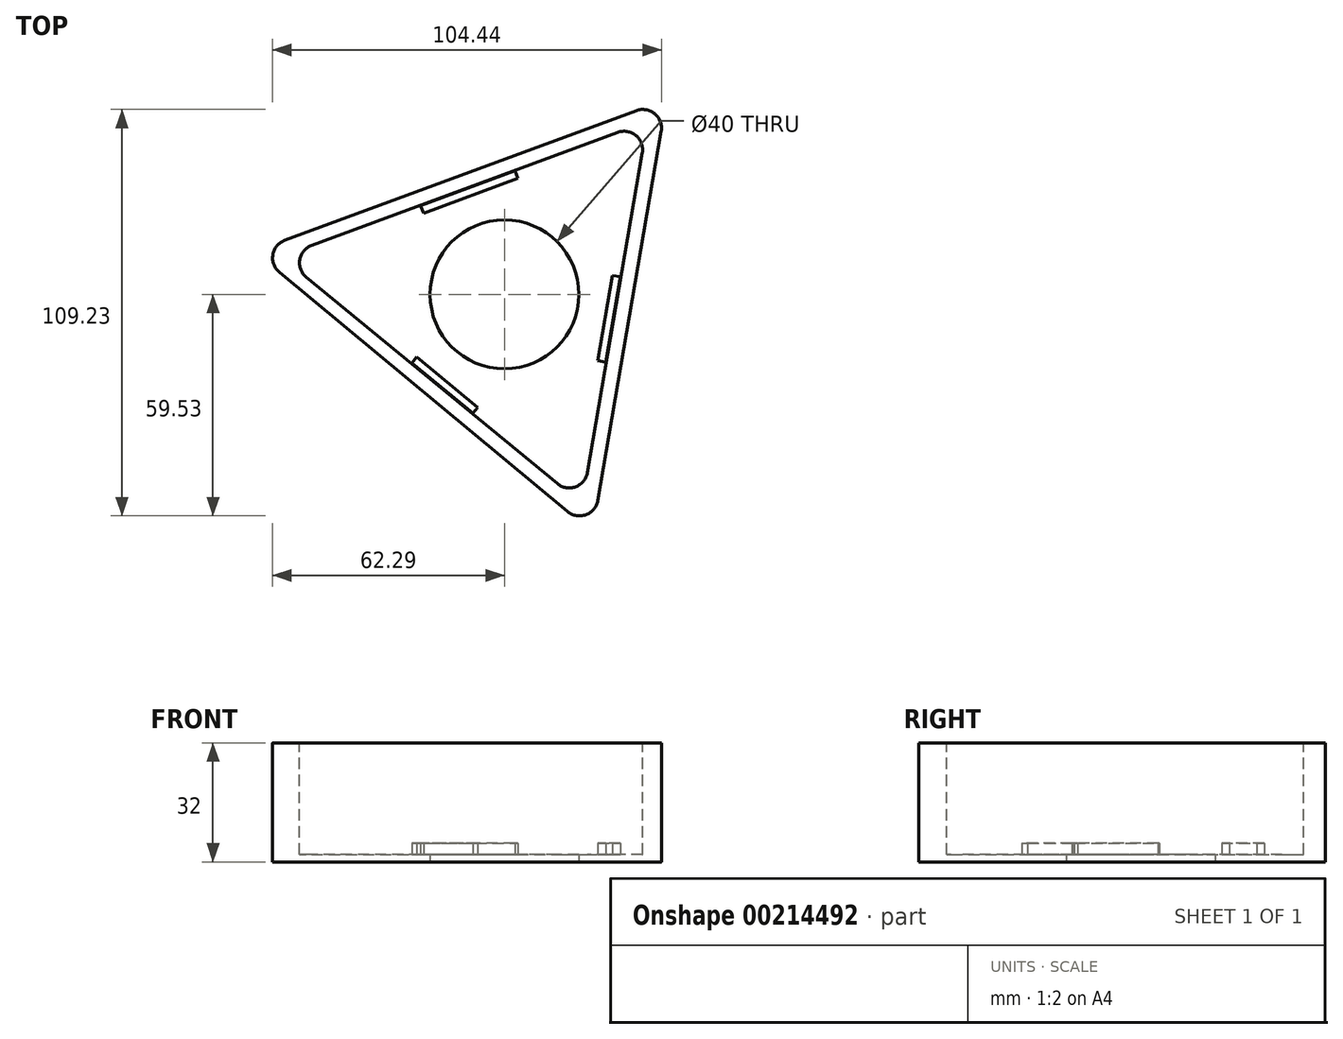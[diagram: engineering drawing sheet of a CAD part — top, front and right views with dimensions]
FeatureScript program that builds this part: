
annotation { "Feature Type Name" : "Feature", "Feature Type Description" : "" }
export const myFeature = defineFeature(function(context is Context, id is Id, definition is map)
    precondition{}
    {
        {
            var Q0;
            Q0=qCreatedBy(makeId("Top.planeOp"),FACE);
            var sketch = newSketch(context, id + "F0", { "sketchPlane" : qUnion([Q0])});
            skCircle(sketch, "E0.cCircle", {"center": v(0, 0) * mm, "radius": 34.06 * mm, "construction": true});
            skLineSegment(sketch, "E0.0", {"start": v(43.55, 52.4) * mm, "end": v(23.6, -63.9) * mm});
            skLineSegment(sketch, "E0.1", {"start": v(23.6, -63.9) * mm, "end": v(-67.15, 11.52) * mm});
            skLineSegment(sketch, "E0.2", {"start": v(-67.15, 11.52) * mm, "end": v(43.55, 52.4) * mm});
            skPoint(sketch, "E0.0.midPoint", {"position": v(33.57, -5.76) * mm});
            skCircle(sketch, "E1", {"center": v(0, 0) * mm, "radius": 20 * mm});
            skSolve(sketch);
        }
        {
            var Q0;
            Q0=makeQuery(id+"F0.imprint","IMPRINT",FACE,{"disambiguationData":[TD([[makeQuery(id+"F0.imprint","IMPRINT",EDGE,{"derivedFrom":sQuery(id+"F0.wireOp",EDGE,"E0.0")}),-1.0]])]});
            extrude(context, id + "F1", {"entities" : qUnion([Q0]), "depth" : 2 * mm});
        }
        {
            var Q0;
            Q0=makeQuery(id+"F1.opExtrude","CAP_FACE",FACE,{"disambiguationData":[OSD([sQuery(id+"F0.wireOp",EDGE,"E0.0"),sQuery(id+"F0.wireOp",EDGE,"E0.1"),sQuery(id+"F0.wireOp",EDGE,"E0.2"),sQuery(id+"F0.wireOp",EDGE,"E1")])],"isStart":false});
            var sketch = newSketch(context, id + "F2", { "sketchPlane" : qUnion([Q0])});
            skLineSegment(sketch, "E2", {"start": v(-59.98, 10.17) * mm, "end": v(38.5, 46.54) * mm});
            skLineSegment(sketch, "E3", {"start": v(38.5, 46.54) * mm, "end": v(20.85, -56.35) * mm});
            skLineSegment(sketch, "E4", {"start": v(20.85, -56.35) * mm, "end": v(-59.98, 10.17) * mm});
            skSolve(sketch);
        }
        {
            var Q0;
            Q0=makeQuery(id+"F2.imprint","IMPRINT",FACE,{"disambiguationData":[TD([[makeQuery(id+"F2.imprint","IMPRINT",EDGE,{"derivedFrom":sQuery(id+"F2.wireOp",EDGE,"E2")}),1.0]])]});
            extrude(context, id + "F3", {"entities" : qUnion([Q0]), "operationType" : NewBodyOperationType.ADD, "depth" : 30 * mm});
        }
        {
            var Q0;
            {var subQ0=sQuery(id+"F0.wireOp",EDGE,"E0.2");var subQ1=sQuery(id+"F0.wireOp",EDGE,"E0.1");Q0=makeQuery(id+"F3.boolean.opBoolean","MERGE",EDGE,{"derivedFrom":[makeQuery(id+"F1.opExtrude","SWEPT_EDGE",EDGE,{"disambiguationData":[OSD([subQ1,subQ0])]}),makeQuery(id+"F3.opExtrude","SWEPT_EDGE",EDGE,{"disambiguationData":[OSD([subQ1,subQ0])]})]});}
            var Q1;
            {var subQ0=sQuery(id+"F0.wireOp",EDGE,"E0.2");var subQ1=sQuery(id+"F0.wireOp",EDGE,"E0.0");Q1=makeQuery(id+"F3.boolean.opBoolean","MERGE",EDGE,{"derivedFrom":[makeQuery(id+"F1.opExtrude","SWEPT_EDGE",EDGE,{"disambiguationData":[OSD([subQ1,subQ0])]}),makeQuery(id+"F3.opExtrude","SWEPT_EDGE",EDGE,{"disambiguationData":[OSD([subQ1,subQ0])]})]});}
            var Q2;
            {var subQ0=sQuery(id+"F0.wireOp",EDGE,"E0.1");var subQ1=sQuery(id+"F0.wireOp",EDGE,"E0.0");Q2=makeQuery(id+"F3.boolean.opBoolean","MERGE",EDGE,{"derivedFrom":[makeQuery(id+"F1.opExtrude","SWEPT_EDGE",EDGE,{"disambiguationData":[OSD([subQ1,subQ0])]}),makeQuery(id+"F3.opExtrude","SWEPT_EDGE",EDGE,{"disambiguationData":[OSD([subQ1,subQ0])]})]});}
            fillet(context, id + "F4", {"entities" : qUnion([Q0, Q1, Q2]), "radius" : 5 * mm, "tangentPropagation" : true, "allowEdgeOverflow" : false});
        }
        {
            var Q0;
            Q0=makeQuery(id+"F3.opExtrude","SWEPT_EDGE",EDGE,{"disambiguationData":[OSD([sQuery(id+"F2.wireOp",EDGE,"E2"),sQuery(id+"F2.wireOp",EDGE,"E4")])]});
            var Q1;
            Q1=makeQuery(id+"F3.opExtrude","SWEPT_EDGE",EDGE,{"disambiguationData":[OSD([sQuery(id+"F2.wireOp",EDGE,"E2"),sQuery(id+"F2.wireOp",EDGE,"E3")])]});
            var Q2;
            Q2=makeQuery(id+"F3.opExtrude","SWEPT_EDGE",EDGE,{"disambiguationData":[OSD([sQuery(id+"F2.wireOp",EDGE,"E3"),sQuery(id+"F2.wireOp",EDGE,"E4")])]});
            fillet(context, id + "F5", {"entities" : qUnion([Q0, Q1, Q2]), "radius" : 5 * mm, "tangentPropagation" : true, "allowEdgeOverflow" : false});
        }
        {
            var Q0;
            Q0 = qSketchRegion(id + "F0", true);
            extrude(context, id + "F6", {"entities" : qUnion([Q0]), "depth" : 2 * mm});
        }
        {
            var Q0;
            Q0=makeQuery(id+"F6.opExtrude","SWEPT_EDGE",EDGE,{"disambiguationData":[OSD([sQuery(id+"F0.wireOp",EDGE,"E0.1"),sQuery(id+"F0.wireOp",EDGE,"E0.2")])]});
            var Q1;
            Q1=makeQuery(id+"F6.opExtrude","SWEPT_EDGE",EDGE,{"disambiguationData":[OSD([sQuery(id+"F0.wireOp",EDGE,"E0.0"),sQuery(id+"F0.wireOp",EDGE,"E0.1")])]});
            var Q2;
            Q2=makeQuery(id+"F6.opExtrude","SWEPT_EDGE",EDGE,{"disambiguationData":[OSD([sQuery(id+"F0.wireOp",EDGE,"E0.0"),sQuery(id+"F0.wireOp",EDGE,"E0.2")])]});
            fillet(context, id + "F7", {"entities" : qUnion([Q0, Q1, Q2]), "radius" : 5 * mm, "tangentPropagation" : true, "allowEdgeOverflow" : false});
        }
        {
            var Q0;
            Q0=makeQuery(id+"F2.imprint","IMPRINT",FACE,{"disambiguationData":[TD([[makeQuery(id+"F2.imprint","IMPRINT",EDGE,{"derivedFrom":sQuery(id+"F2.wireOp",EDGE,"E2")}),-1.0]])]});
            var sketch = newSketch(context, id + "F8", { "sketchPlane" : qUnion([Q0])});
            skLineSegment(sketch, "E5", {"start": v(-22.6, 23.84) * mm, "end": v(-21.64, 21.81) * mm});
            skLineSegment(sketch, "E6", {"start": v(-21.64, 21.81) * mm, "end": v(3.55, 31.24) * mm});
            skLineSegment(sketch, "E7", {"start": v(3.55, 31.24) * mm, "end": v(2.78, 33.28) * mm});
            skLineSegment(sketch, "E8", {"start": v(2.78, 33.28) * mm, "end": v(-22.6, 23.84) * mm});
            skLineSegment(sketch, "E9", {"start": v(31.13, 4.74) * mm, "end": v(27.19, -18.18) * mm});
            skLineSegment(sketch, "E10", {"start": v(27.19, -18.18) * mm, "end": v(25.06, -17.82) * mm});
            skLineSegment(sketch, "E11", {"start": v(25.06, -17.82) * mm, "end": v(28.98, 5.04) * mm});
            skLineSegment(sketch, "E12", {"start": v(28.98, 5.04) * mm, "end": v(31.13, 4.74) * mm});
            skLineSegment(sketch, "E13", {"start": v(-24.86, -18.42) * mm, "end": v(-8.5, -31.91) * mm});
            skLineSegment(sketch, "E14", {"start": v(-8.5, -31.91) * mm, "end": v(-7.2, -30.33) * mm});
            skLineSegment(sketch, "E15", {"start": v(-7.2, -30.33) * mm, "end": v(-23.57, -16.84) * mm});
            skLineSegment(sketch, "E16", {"start": v(-23.57, -16.84) * mm, "end": v(-24.86, -18.42) * mm});
            skSolve(sketch);
        }
        {
            var Q0;
            Q0=makeQuery(id+"F8.imprint","IMPRINT",FACE,{"disambiguationData":[TD([[makeQuery(id+"F8.imprint","IMPRINT",EDGE,{"derivedFrom":sQuery(id+"F8.wireOp",EDGE,"E13")}),1.0]])]});
            var Q1;
            Q1=makeQuery(id+"F8.imprint","IMPRINT",FACE,{"disambiguationData":[TD([[makeQuery(id+"F8.imprint","IMPRINT",EDGE,{"derivedFrom":sQuery(id+"F8.wireOp",EDGE,"E5")}),1.0]])]});
            var Q2;
            Q2=makeQuery(id+"F8.imprint","IMPRINT",FACE,{"disambiguationData":[TD([[makeQuery(id+"F8.imprint","IMPRINT",EDGE,{"derivedFrom":sQuery(id+"F8.wireOp",EDGE,"E9")}),-1.0]])]});
            extrude(context, id + "F9", {"entities" : qUnion([Q0, Q1, Q2]), "operationType" : NewBodyOperationType.ADD, "depth" : 3 * mm});
        }
    });
